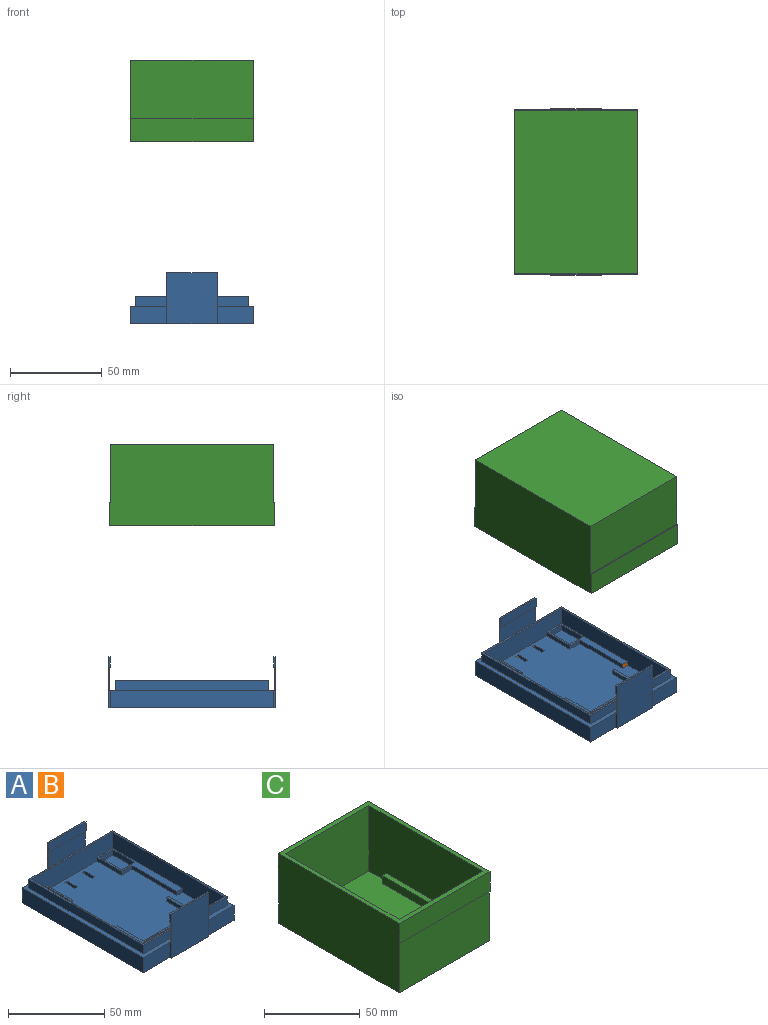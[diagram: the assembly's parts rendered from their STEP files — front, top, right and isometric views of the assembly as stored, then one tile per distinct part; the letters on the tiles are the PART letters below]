
ASSEMBLY  parts=3 mates=1
PART A: 107 faces, bbox 66.7x90.9x27.9 mm
  f0: plane 27.31x5.72mm, normal (0,1,0), area 156mm2, adj f1,f87,f88,f90
  f1: plane 27.94x1mm, normal (-1,0,0), area 21.5mm2, adj f0,f8,f9,f13,f88,f89,f90,f91
  f2: plane 19.69x9.53mm, normal (0,-1,0), area 187.5mm2, adj f8,f10,f13,f87
  f3: plane 27.31x5.72mm, normal (0,-1,0), area 156mm2, adj f4,f82,f83,f85
  f4: plane 27.94x1mm, normal (1,0,0), area 21.5mm2, adj f3,f5,f8,f13,f83,f84,f85,f86
  f5: plane 19.69x9.53mm, normal (0,1,0), area 187.5mm2, adj f4,f8,f10,f13
  f6: plane 81.82x59.6mm, normal (0,0,1), area 3640.6mm2, adj f14,f15,f17,f18,f19,f20,f21,f22
  f7: plane 51.07x11.7mm, normal (0,0,1), area 187.7mm2, adj f17,f18,f41,f42,f43,f44,f76,f77
  f8: plane 90.9x66.68mm, normal (0,0,-1), area 5954.5mm2, adj f1,f2,f4,f5,f9,f10,f11,f12
  f9: plane 19.69x9.53mm, normal (0,-1,0), area 187.5mm2, adj f1,f8,f12,f13
  f10: plane 88.9x9.53mm, normal (1,0,0), area 846.8mm2, adj f2,f5,f8,f13
  f11: plane 19.69x9.53mm, normal (0,1,0), area 187.5mm2, adj f8,f12,f13,f82
  f12: plane 88.9x9.53mm, normal (-1,0,0), area 846.8mm2, adj f8,f9,f11,f13
  f13: plane 89.92x66.68mm, normal (0,0,1), area 792.3mm2, adj f1,f2,f4,f5,f9,f10,f11,f12
  f14: plane 18.05x2.46mm, normal (-1,0,0), area 44.4mm2, adj f6,f15,f16,f77
  f15: plane 7.7x2.46mm, normal (0,-1,0), area 18.9mm2, adj f6,f14,f16,f81
  f16: plane 51.07x11.7mm, normal (0,0,1), area 187.7mm2, adj f14,f15,f37,f38,f39,f40,f70,f77
  f17: plane 18.05x2.46mm, normal (1,0,0), area 44.4mm2, adj f6,f7,f18,f77
  f18: plane 7.7x2.46mm, normal (0,-1,0), area 18.9mm2, adj f6,f7,f17,f79
  f19: plane 19.05x2.46mm, normal (-1,0,0), area 46.9mm2, adj f6,f20,f25,f26
  f20: plane 36.2x2.46mm, normal (0,1,0), area 89mm2, adj f6,f19,f21,f26
  f21: plane 19.05x2.46mm, normal (1,0,0), area 46.9mm2, adj f6,f20,f22,f26
  f22: plane 2.46x1.59mm, normal (0,1,0), area 3.9mm2, adj f6,f21,f23,f26
  f23: plane 30.75x2.46mm, normal (-1,0,0), area 75.6mm2, adj f6,f22,f26,f69
  f24: plane 30.75x2.46mm, normal (1,0,0), area 75.6mm2, adj f6,f25,f26,f69
  f25: plane 2.46x1.59mm, normal (0,1,0), area 3.9mm2, adj f6,f19,f24,f26
  f26: plane 39.37x30.75mm, normal (0,0,1), area 158.6mm2, adj f19,f20,f21,f22,f23,f24,f25,f45
  f27: plane 2.54x1.91mm, normal (0,1,0), area 4.8mm2, adj f6,f8,f28,f30
  f28: plane 7.24x2.54mm, normal (-1,0,0), area 18.4mm2, adj f6,f8,f27,f29
  f29: plane 2.54x1.91mm, normal (0,-1,0), area 4.8mm2, adj f6,f8,f28,f30
  f30: plane 7.24x2.54mm, normal (1,0,0), area 18.4mm2, adj f6,f8,f27,f29
  f31: plane 7.25x2.54mm, normal (1,0,0), area 18.4mm2, adj f6,f8,f32,f34
  f32: plane 2.54x1.9mm, normal (0,1,0), area 4.8mm2, adj f6,f8,f31,f33
  f33: plane 7.25x2.54mm, normal (-1,0,0), area 18.4mm2, adj f6,f8,f32,f34
  f34: plane 2.54x1.9mm, normal (0,-1,0), area 4.8mm2, adj f6,f8,f31,f33
  f35: plane 81.82x59.6mm, normal (0,0,-1), area 3865.6mm2, adj f37,f38,f39,f40,f41,f42,f43,f44
  f36: plane 81.82x59.6mm, normal (0,0,1), area 4539.5mm2, adj f49,f50,f51,f52,f53,f54,f55,f56
  f37: plane 16.05x3.46mm, normal (-1,0,0), area 55.5mm2, adj f16,f35,f38,f40
  f38: plane 9.7x3.46mm, normal (0,-1,0), area 33.6mm2, adj f16,f35,f37,f39
  f39: plane 16.05x3.46mm, normal (1,0,0), area 55.5mm2, adj f16,f35,f38,f40
  f40: plane 9.7x3.46mm, normal (0,1,0), area 33.6mm2, adj f16,f35,f37,f39
  f41: plane 16.05x3.46mm, normal (-1,0,0), area 55.5mm2, adj f7,f35,f42,f44
  f42: plane 9.7x3.46mm, normal (0,-1,0), area 33.6mm2, adj f7,f35,f41,f43
  f43: plane 16.05x3.46mm, normal (1,0,0), area 55.5mm2, adj f7,f35,f42,f44
  f44: plane 9.7x3.46mm, normal (0,1,0), area 33.6mm2, adj f7,f35,f41,f43
  f45: plane 37.37x3.46mm, normal (0,-1,0), area 129.3mm2, adj f26,f35,f46,f48
  f46: plane 9.7x3.46mm, normal (1,0,0), area 33.6mm2, adj f26,f35,f45,f47
  f47: plane 37.37x3.46mm, normal (0,1,0), area 129.3mm2, adj f26,f35,f46,f48
  f48: plane 9.7x3.46mm, normal (-1,0,0), area 33.6mm2, adj f26,f35,f45,f47
  f49: plane 3.91x0.54mm, normal (0,-1,0), area 2.1mm2, adj f35,f36,f50,f52
  f50: plane 9.24x0.54mm, normal (1,0,0), area 5mm2, adj f35,f36,f49,f51
  f51: plane 3.91x0.54mm, normal (0,1,0), area 2.1mm2, adj f35,f36,f50,f52
  f52: plane 9.24x0.54mm, normal (-1,0,0), area 5mm2, adj f35,f36,f49,f51
  f53: plane 9.25x0.54mm, normal (-1,0,0), area 5mm2, adj f35,f36,f54,f56
  f54: plane 3.9x0.54mm, normal (0,-1,0), area 2.1mm2, adj f35,f36,f53,f55
  f55: plane 9.25x0.54mm, normal (1,0,0), area 5mm2, adj f35,f36,f54,f56
  f56: plane 3.9x0.54mm, normal (0,1,0), area 2.1mm2, adj f35,f36,f53,f55
  f57: plane 59.6x0.54mm, normal (0,-1,0), area 32.2mm2, adj f35,f36,f61,f67
  f58: plane 4x0.54mm, normal (0,1,0), area 2.2mm2, adj f35,f36,f59,f61
  f59: plane 33.02x0.54mm, normal (1,0,0), area 17.8mm2, adj f35,f36,f58,f60
  f60: plane 4x0.54mm, normal (0,-1,0), area 2.2mm2, adj f35,f36,f59,f63
  f61: plane 18.05x0.54mm, normal (1,0,0), area 9.7mm2, adj f35,f36,f57,f58
  f62: plane 59.6x0.54mm, normal (0,1,0), area 32.2mm2, adj f35,f36,f63,f68
  f63: plane 30.75x0.54mm, normal (1,0,0), area 16.6mm2, adj f35,f36,f60,f62
  f64: plane 33.02x0.54mm, normal (-1,0,0), area 17.8mm2, adj f35,f36,f65,f66
  f65: plane 4x0.54mm, normal (0,1,0), area 2.2mm2, adj f35,f36,f64,f67
  f66: plane 4x0.54mm, normal (0,-1,0), area 2.2mm2, adj f35,f36,f64,f68
  f67: plane 18.05x0.54mm, normal (-1,0,0), area 9.7mm2, adj f35,f36,f57,f65
  f68: plane 30.75x0.54mm, normal (-1,0,0), area 16.6mm2, adj f35,f36,f62,f66
  f69: plane 59.6x12.46mm, normal (0,1,0), area 645.7mm2, adj f6,f23,f24,f26,f70,f75,f76
  f70: plane 81.82x12.46mm, normal (-1,0,0), area 893.8mm2, adj f6,f16,f69,f75,f77,f80
  f71: plane 83.82x5.48mm, normal (-1,0,0), area 458.9mm2, adj f13,f72,f74,f75
  f72: plane 61.6x5.48mm, normal (0,-1,0), area 337.2mm2, adj f13,f71,f73,f75
  f73: plane 83.82x5.48mm, normal (1,0,0), area 458.9mm2, adj f13,f72,f74,f75
  f74: plane 61.6x5.48mm, normal (0,1,0), area 337.2mm2, adj f13,f71,f73,f75
  f75: plane 83.82x61.6mm, normal (0,0,1), area 286.8mm2, adj f69,f70,f71,f72,f73,f74,f76,f77
  f76: plane 81.82x12.46mm, normal (1,0,0), area 893.8mm2, adj f6,f7,f69,f75,f77,f78
  f77: plane 59.6x12.46mm, normal (0,-1,0), area 685mm2, adj f6,f7,f14,f16,f17,f70,f75,f76
  f78: plane 4x2.46mm, normal (0,-1,0), area 9.8mm2, adj f6,f7,f76,f79
  f79: plane 33.02x2.46mm, normal (1,0,0), area 81.2mm2, adj f6,f7,f18,f78
  f80: plane 4x2.46mm, normal (0,-1,0), area 9.8mm2, adj f6,f16,f70,f81
  f81: plane 33.02x2.46mm, normal (-1,0,0), area 81.2mm2, adj f6,f15,f16,f80
  f82: plane 27.94x1mm, normal (-1,0,0), area 21.5mm2, adj f3,f8,f11,f13,f83,f84,f85,f86
  f83: plane 27.31x1mm, normal (0,0,1), area 27.3mm2, adj f3,f4,f82,f84
  f84: plane 27.94x27.31mm, normal (0,1,0), area 762.9mm2, adj f4,f8,f82,f83
  f85: plane 27.31x0.51mm, normal (0,0,-1), area 13.9mm2, adj f3,f4,f82,f86
  f86: plane 27.31x12.7mm, normal (0,-1,0), area 346.8mm2, adj f4,f13,f82,f85
  f87: plane 27.94x1mm, normal (1,0,0), area 21.5mm2, adj f0,f2,f8,f13,f88,f89,f90,f91
  f88: plane 27.31x1mm, normal (0,0,1), area 27.3mm2, adj f0,f1,f87,f89
  f89: plane 27.94x27.31mm, normal (0,-1,0), area 762.9mm2, adj f1,f8,f87,f88
  f90: plane 27.31x0.51mm, normal (0,0,-1), area 13.9mm2, adj f0,f1,f87,f91
  f91: plane 27.31x12.7mm, normal (0,1,0), area 346.8mm2, adj f1,f13,f87,f90
  f92: plane 61.6x0.54mm, normal (0,1,0), area 33.3mm2, adj f93,f95,f100,f106
  f93: plane 83.82x0.54mm, normal (1,0,0), area 45.3mm2, adj f92,f94,f100,f106
  f94: plane 61.6x0.54mm, normal (0,-1,0), area 33.3mm2, adj f93,f95,f100,f106
  f95: plane 83.82x0.54mm, normal (-1,0,0), area 45.3mm2, adj f92,f94,f100,f106
  f96: plane 85.82x6.99mm, normal (1,0,0), area 599.5mm2, adj f97,f99,f100,f101
  f97: plane 63.6x6.99mm, normal (0,1,0), area 444.2mm2, adj f96,f98,f100,f101
  f98: plane 85.82x6.99mm, normal (-1,0,0), area 599.5mm2, adj f97,f99,f100,f101
  f99: plane 63.6x6.99mm, normal (0,-1,0), area 444.2mm2, adj f96,f98,f100,f101
  f100: plane 85.82x63.6mm, normal (0,0,-1), area 294.8mm2, adj f92,f93,f94,f95,f96,f97,f98,f99
  f101: plane 86.9x64.68mm, normal (0,0,-1), area 162.5mm2, adj f96,f97,f98,f99,f102,f103,f104,f105
  f102: plane 86.9x7.53mm, normal (1,0,0), area 653.9mm2, adj f101,f103,f105,f106
  f103: plane 64.68x7.53mm, normal (0,-1,0), area 486.7mm2, adj f101,f102,f104,f106
  f104: plane 86.9x7.53mm, normal (-1,0,0), area 653.9mm2, adj f101,f103,f105,f106
  f105: plane 64.68x7.53mm, normal (0,1,0), area 486.7mm2, adj f101,f102,f104,f106
  f106: plane 86.9x64.68mm, normal (0,0,1), area 457.4mm2, adj f92,f93,f94,f95,f102,f103,f104,f105
PART B: same geometry as A
PART C: 27 faces, bbox 66.7x89.9x44.5 mm
  f0: plane 66.68x31.75mm, normal (0,1,0), area 2116.9mm2, adj f7,f9,f10,f23
  f1: plane 61.6x54.23mm, normal (0,0,1), area 3087.1mm2, adj f2,f3,f4,f11,f12,f15,f17,f21
  f2: plane 50.8x5.08mm, normal (1,0,0), area 248.4mm2, adj f1,f5,f14,f15,f16,f20,f21,f22
  f3: plane 50.8x5.08mm, normal (-1,0,0), area 248.4mm2, adj f1,f5,f17,f18,f19,f20,f21,f22
  f4: plane 83.82x41.91mm, normal (-1,0,0), area 3254.8mm2, adj f1,f5,f6,f11,f13,f17,f18,f19
  f5: plane 61.6x26.42mm, normal (0,0,1), area 1589.9mm2, adj f2,f3,f4,f12,f13,f14,f18,f20
  f6: plane 89.9x66.68mm, normal (0,0,1), area 831.2mm2, adj f4,f7,f9,f11,f12,f13,f24,f26
  f7: plane 89.9x44.45mm, normal (-1,0,0), area 3964.3mm2, adj f0,f6,f8,f10,f23,f24,f25,f26
  f8: plane 66.68x31.75mm, normal (0,-1,0), area 2117.2mm2, adj f7,f9,f10,f25
  f9: plane 89.9x44.45mm, normal (1,0,0), area 3964.3mm2, adj f0,f6,f8,f10,f23,f24,f25,f26
  f10: plane 88.9x66.68mm, normal (0,0,-1), area 5927.4mm2, adj f0,f7,f8,f9
  f11: plane 61.6x41.91mm, normal (0,-1,0), area 2581.4mm2, adj f1,f4,f6,f12
  f12: plane 83.82x41.91mm, normal (1,0,0), area 3254.8mm2, adj f1,f5,f6,f11,f13,f14,f15,f16
  f13: plane 61.6x41.91mm, normal (0,1,0), area 2581.4mm2, adj f4,f5,f6,f12
  f14: plane 5.08x3.05mm, normal (0,-1,0), area 15.5mm2, adj f2,f5,f12,f16
  f15: plane 5.08x3.05mm, normal (0,1,0), area 15.5mm2, adj f1,f2,f12,f16
  f16: plane 50.8x3.05mm, normal (0,0,1), area 154.8mm2, adj f2,f12,f14,f15
  f17: plane 5.08x3.05mm, normal (0,1,0), area 15.5mm2, adj f1,f3,f4,f19
  f18: plane 5.08x3.05mm, normal (0,-1,0), area 15.5mm2, adj f3,f4,f5,f19
  f19: plane 50.8x3.05mm, normal (0,0,1), area 154.8mm2, adj f3,f4,f17,f18
  f20: plane 55.5x3.05mm, normal (0,-1,0), area 169.2mm2, adj f2,f3,f5,f22
  f21: plane 55.5x3.05mm, normal (0,1,0), area 169.2mm2, adj f1,f2,f3,f22
  f22: plane 55.5x3.18mm, normal (0,0,1), area 176.2mm2, adj f2,f3,f20,f21
  f23: plane 66.68x0.5mm, normal (0,0,-1), area 33.3mm2, adj f0,f7,f9,f24
  f24: plane 66.68x12.7mm, normal (0,1,0), area 846.8mm2, adj f6,f7,f9,f23
  f25: plane 66.68x0.5mm, normal (0,0,-1), area 33.3mm2, adj f7,f8,f9,f26
  f26: plane 66.68x12.7mm, normal (0,-1,0), area 846.5mm2, adj f6,f7,f9,f25
PLACE A t=(27.91,-55.59,176.81)mm
PLACE B t=(27.91,-55.59,176.81)mm
PLACE C rot(axis=(0,-1,0),180deg) t=(26.79,-56.29,320.64)mm
MATE cylindrical C.f6 <-> B.f13  axis (0,0,-1) through (58.71,-45.43,276.19)mm
